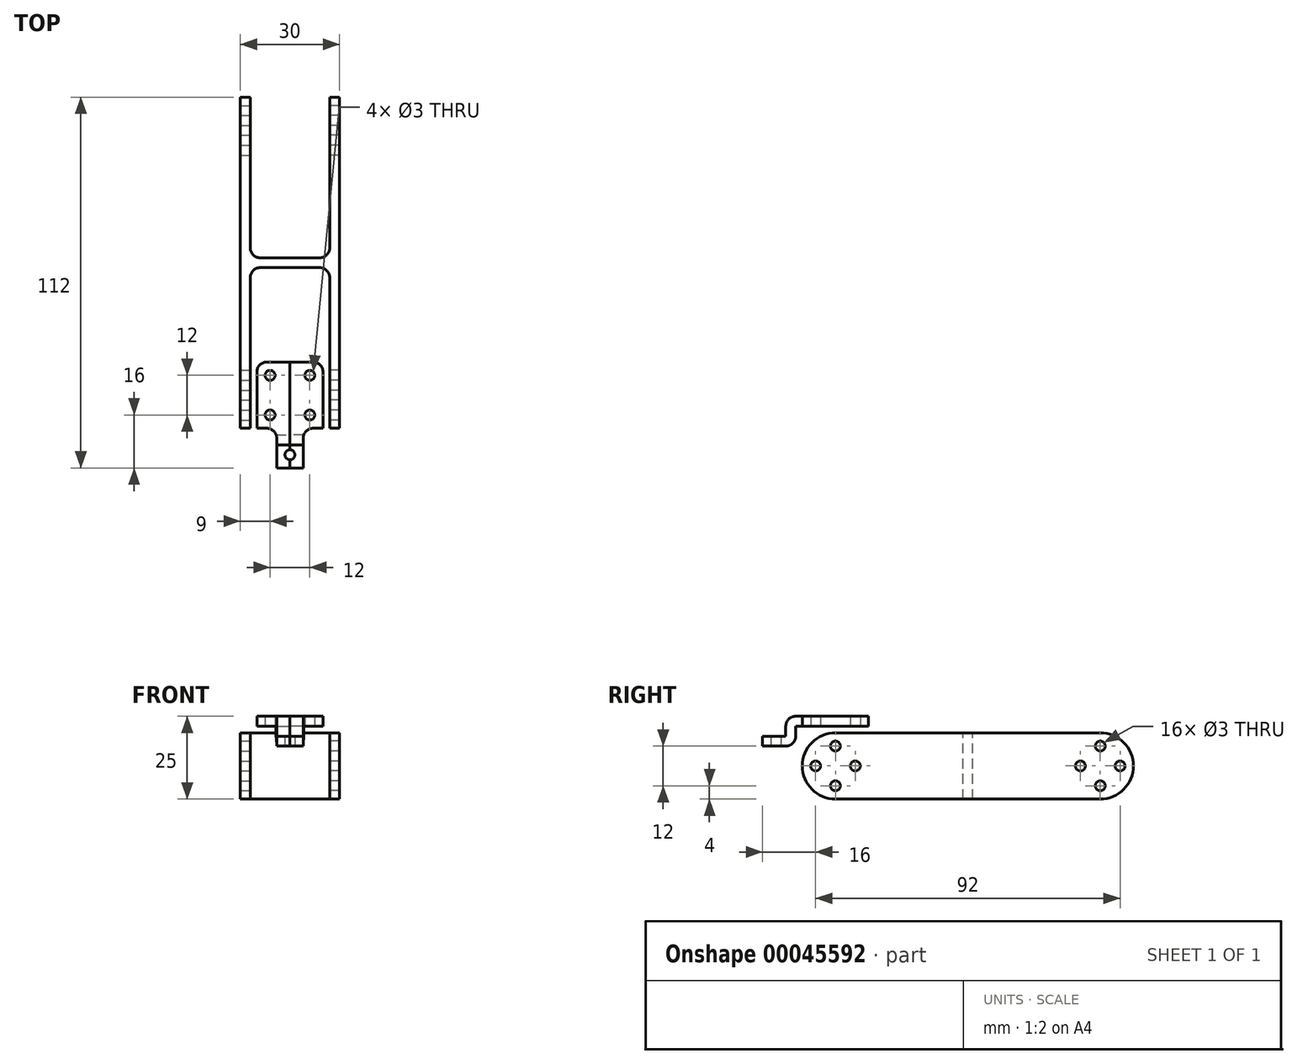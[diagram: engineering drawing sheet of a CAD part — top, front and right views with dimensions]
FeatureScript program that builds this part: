
annotation { "Feature Type Name" : "Feature", "Feature Type Description" : "" }
export const myFeature = defineFeature(function(context is Context, id is Id, definition is map)
    precondition{}
    {
        {
            var Q0;
            Q0=qCreatedBy(makeId("Right.planeOp"),FACE);
            var sketch = newSketch(context, id + "F0", { "sketchPlane" : qUnion([Q0])});
            skLineSegment(sketch, "E0.rect.bottom", {"start": v(12, 88) * mm, "end": v(-12, 88) * mm});
            skLineSegment(sketch, "E0.rect.top", {"start": v(12, 112) * mm, "end": v(-12, 112) * mm});
            skLineSegment(sketch, "E0.rect.left", {"start": v(12, 88) * mm, "end": v(12, 112) * mm});
            skLineSegment(sketch, "E0.rect.right", {"start": v(-12, 88) * mm, "end": v(-12, 112) * mm});
            skPoint(sketch, "E0.rect.middle", {"position": v(0, 100) * mm});
            skLineSegment(sketch, "E1.rect.bottom", {"start": v(-68, 88) * mm, "end": v(-92, 88) * mm});
            skLineSegment(sketch, "E1.rect.top", {"start": v(-68, 112) * mm, "end": v(-92, 112) * mm});
            skLineSegment(sketch, "E1.rect.left", {"start": v(-68, 88) * mm, "end": v(-68, 112) * mm});
            skLineSegment(sketch, "E1.rect.right", {"start": v(-92, 88) * mm, "end": v(-92, 112) * mm});
            skPoint(sketch, "E1.rect.middle", {"position": v(-80, 100) * mm});
            skLineSegment(sketch, "E2.rect.bottom", {"start": v(-92, 94) * mm, "end": v(-104, 94) * mm});
            skLineSegment(sketch, "E2.rect.top", {"start": v(-92, 106) * mm, "end": v(-104, 106) * mm});
            skLineSegment(sketch, "E2.rect.left", {"start": v(-92, 94) * mm, "end": v(-92, 106) * mm});
            skLineSegment(sketch, "E2.rect.right", {"start": v(-104, 94) * mm, "end": v(-104, 106) * mm});
            skPoint(sketch, "E2.rect.middle", {"position": v(-98, 100) * mm});
            skLineSegment(sketch, "E3", {"start": v(0, 100) * mm, "end": v(-80, 100) * mm, "construction": true});
            skLineSegment(sketch, "E4", {"start": v(-80, 100) * mm, "end": v(-98, 100) * mm, "construction": true});
            skLineSegment(sketch, "E5.rect.bottom", {"start": v(-18, 0) * mm, "end": v(18, 0) * mm});
            skLineSegment(sketch, "E5.rect.top", {"start": v(-18, -36) * mm, "end": v(18, -36) * mm});
            skLineSegment(sketch, "E5.rect.left", {"start": v(-18, 0) * mm, "end": v(-18, -36) * mm});
            skLineSegment(sketch, "E5.rect.right", {"start": v(18, 0) * mm, "end": v(18, -36) * mm});
            skPoint(sketch, "E5.rect.middle", {"position": v(0, -18) * mm});
            skCircle(sketch, "E6", {"center": v(0, 100) * mm, "radius": 6 * mm, "construction": true});
            skCircle(sketch, "E7", {"center": v(-80, 100) * mm, "radius": 6 * mm, "construction": true});
            skCircle(sketch, "E8", {"center": v(-80, 106) * mm, "radius": 1.5 * mm});
            skCircle(sketch, "E9", {"center": v(0, 106) * mm, "radius": 1.5 * mm});
            skCircle(sketch, "E10", {"center": v(-98, 100) * mm, "radius": 1.5 * mm});
            skCircle(sketch, "E11.1.0", {"center": v(-86, 100) * mm, "radius": 1.5 * mm});
            skCircle(sketch, "E11.2.0", {"center": v(-80, 94) * mm, "radius": 1.5 * mm});
            skCircle(sketch, "E11.3.0", {"center": v(-74, 100) * mm, "radius": 1.5 * mm});
            skCircle(sketch, "E12.1.0", {"center": v(-6, 100) * mm, "radius": 1.5 * mm});
            skCircle(sketch, "E12.2.0", {"center": v(0, 94) * mm, "radius": 1.5 * mm});
            skCircle(sketch, "E12.3.0", {"center": v(6, 100) * mm, "radius": 1.5 * mm});
            skLineSegment(sketch, "E13.0", {"start": v(-12, -6) * mm, "end": v(12, -6) * mm, "construction": true});
            skLineSegment(sketch, "E13.1", {"start": v(-12, -6) * mm, "end": v(-12, -30) * mm, "construction": true});
            skLineSegment(sketch, "E13.2", {"start": v(-12, -30) * mm, "end": v(12, -30) * mm, "construction": true});
            skLineSegment(sketch, "E13.3", {"start": v(12, -6) * mm, "end": v(12, -30) * mm, "construction": true});
            skCircle(sketch, "E14", {"center": v(-12, -6) * mm, "radius": 1.5 * mm});
            skCircle(sketch, "E15", {"center": v(12, -6) * mm, "radius": 1.5 * mm});
            skCircle(sketch, "E16", {"center": v(12, -30) * mm, "radius": 1.5 * mm});
            skCircle(sketch, "E17", {"center": v(-12, -30) * mm, "radius": 1.5 * mm});
            skSolve(sketch);
        }
        {
            var Q0;
            Q0=qCreatedBy(makeId("Top.planeOp"),FACE);
            var Q1;
            Q1=sQuery(id+"F0.wireOp",VERTEX,"E0.rect.middle");
            cPlane(context, id + "F1", {"entities" : qUnion([Q0, Q1]), "cplaneType" : CPlaneType.PLANE_POINT, "offset" : 150 * mm, "width" : 150 * mm, "height" : 150 * mm});
        }
        {
            var Q0;
            Q0=qCreatedBy(id+"F1.planeOp",FACE);
            var sketch = newSketch(context, id + "F2", { "sketchPlane" : qUnion([Q0])});
            skLineSegment(sketch, "E18.rect.bottom", {"start": v(12, 12) * mm, "end": v(-12, 12) * mm});
            skLineSegment(sketch, "E18.rect.top", {"start": v(12, -12) * mm, "end": v(-12, -12) * mm});
            skLineSegment(sketch, "E18.rect.left", {"start": v(12, 12) * mm, "end": v(12, -12) * mm});
            skLineSegment(sketch, "E18.rect.right", {"start": v(-12, 12) * mm, "end": v(-12, -12) * mm});
            skPoint(sketch, "E18.rect.middle", {"position": v(0, 0) * mm});
            skLineSegment(sketch, "E19.rect.bottom", {"start": v(12, -68) * mm, "end": v(-12, -68) * mm});
            skLineSegment(sketch, "E19.rect.top", {"start": v(12, -92) * mm, "end": v(-12, -92) * mm});
            skLineSegment(sketch, "E19.rect.left", {"start": v(12, -68) * mm, "end": v(12, -92) * mm});
            skLineSegment(sketch, "E19.rect.right", {"start": v(-12, -68) * mm, "end": v(-12, -92) * mm});
            skPoint(sketch, "E19.rect.middle", {"position": v(0, -80) * mm});
            skLineSegment(sketch, "E20.rect.bottom", {"start": v(6, -92) * mm, "end": v(-6, -92) * mm});
            skLineSegment(sketch, "E20.rect.top", {"start": v(6, -104) * mm, "end": v(-6, -104) * mm});
            skLineSegment(sketch, "E20.rect.left", {"start": v(6, -92) * mm, "end": v(6, -104) * mm});
            skLineSegment(sketch, "E20.rect.right", {"start": v(-6, -92) * mm, "end": v(-6, -104) * mm});
            skPoint(sketch, "E20.rect.middle", {"position": v(0, -98) * mm});
            skLineSegment(sketch, "E21.0", {"start": v(-6, -74) * mm, "end": v(-6, -86) * mm, "construction": true});
            skLineSegment(sketch, "E21.1", {"start": v(6, -74) * mm, "end": v(-6, -74) * mm, "construction": true});
            skLineSegment(sketch, "E21.2", {"start": v(6, -74) * mm, "end": v(6, -86) * mm, "construction": true});
            skLineSegment(sketch, "E21.3", {"start": v(6, -86) * mm, "end": v(-6, -86) * mm, "construction": true});
            skLineSegment(sketch, "E22.0", {"start": v(-6, 6) * mm, "end": v(-6, -6) * mm, "construction": true});
            skLineSegment(sketch, "E22.1", {"start": v(6, 6) * mm, "end": v(-6, 6) * mm, "construction": true});
            skLineSegment(sketch, "E22.2", {"start": v(6, 6) * mm, "end": v(6, -6) * mm, "construction": true});
            skLineSegment(sketch, "E22.3", {"start": v(6, -6) * mm, "end": v(-6, -6) * mm, "construction": true});
            skCircle(sketch, "E23", {"center": v(-6, -86) * mm, "radius": 1.5 * mm});
            skCircle(sketch, "E24", {"center": v(-6, -74) * mm, "radius": 1.5 * mm});
            skCircle(sketch, "E25", {"center": v(6, -86) * mm, "radius": 1.5 * mm});
            skCircle(sketch, "E26", {"center": v(0, -98) * mm, "radius": 1.5 * mm});
            skCircle(sketch, "E27", {"center": v(6, -74) * mm, "radius": 1.5 * mm});
            skCircle(sketch, "E28", {"center": v(6, -6) * mm, "radius": 1.5 * mm});
            skCircle(sketch, "E29", {"center": v(6, 6) * mm, "radius": 1.5 * mm});
            skCircle(sketch, "E30", {"center": v(-6, 6) * mm, "radius": 1.5 * mm});
            skCircle(sketch, "E31", {"center": v(-6, -6) * mm, "radius": 1.5 * mm});
            skCircle(sketch, "E32", {"center": v(0, -80) * mm, "radius": 1.5 * mm});
            skCircle(sketch, "E33", {"center": v(0, 0) * mm, "radius": 1.5 * mm});
            skSolve(sketch);
        }
        {
            var Q0;
            Q0=qCreatedBy(makeId("Top.planeOp"),FACE);
            var sketch = newSketch(context, id + "F3", { "sketchPlane" : qUnion([Q0])});
            skLineSegment(sketch, "E34.rect.bottom", {"start": v(18, 18) * mm, "end": v(-18, 18) * mm});
            skLineSegment(sketch, "E34.rect.top", {"start": v(18, -18) * mm, "end": v(-18, -18) * mm});
            skLineSegment(sketch, "E34.rect.left", {"start": v(18, 18) * mm, "end": v(18, -18) * mm});
            skLineSegment(sketch, "E34.rect.right", {"start": v(-18, 18) * mm, "end": v(-18, -18) * mm});
            skPoint(sketch, "E34.rect.middle", {"position": v(0, 0) * mm});
            skCircle(sketch, "E35", {"center": v(0, 0) * mm, "radius": 12 * mm, "construction": true});
            skCircle(sketch, "E36", {"center": v(-12, 0) * mm, "radius": 1.5 * mm});
            skCircle(sketch, "E37.1.0", {"center": v(-8.49, -8.49) * mm, "radius": 1.5 * mm});
            skCircle(sketch, "E37.2.0", {"center": v(0, -12) * mm, "radius": 1.5 * mm});
            skCircle(sketch, "E37.3.0", {"center": v(8.49, -8.49) * mm, "radius": 1.5 * mm});
            skCircle(sketch, "E37.4.0", {"center": v(12, 0) * mm, "radius": 1.5 * mm});
            skCircle(sketch, "E37.5.0", {"center": v(8.49, 8.49) * mm, "radius": 1.5 * mm});
            skCircle(sketch, "E37.6.0", {"center": v(0, 12) * mm, "radius": 1.5 * mm});
            skCircle(sketch, "E37.7.0", {"center": v(-8.49, 8.49) * mm, "radius": 1.5 * mm});
            skCircle(sketch, "E38", {"center": v(0, 0) * mm, "radius": 16 * mm});
            skSolve(sketch);
        }
        {
            var Q0;
            Q0=qCreatedBy(makeId("Front.planeOp"),FACE);
            var sketch = newSketch(context, id + "F4", { "sketchPlane" : qUnion([Q0])});
            skLineSegment(sketch, "E39.rect.bottom", {"start": v(12, 88) * mm, "end": v(-12, 88) * mm});
            skLineSegment(sketch, "E39.rect.top", {"start": v(12, 112) * mm, "end": v(-12, 112) * mm});
            skLineSegment(sketch, "E39.rect.left", {"start": v(12, 88) * mm, "end": v(12, 112) * mm});
            skLineSegment(sketch, "E39.rect.right", {"start": v(-12, 88) * mm, "end": v(-12, 112) * mm});
            skPoint(sketch, "E39.rect.middle", {"position": v(0, 100) * mm});
            skLineSegment(sketch, "E40.0", {"start": v(6, 106) * mm, "end": v(-6, 106) * mm, "construction": true});
            skLineSegment(sketch, "E40.1", {"start": v(6, 94) * mm, "end": v(6, 106) * mm, "construction": true});
            skLineSegment(sketch, "E40.2", {"start": v(6, 94) * mm, "end": v(-6, 94) * mm, "construction": true});
            skLineSegment(sketch, "E40.3", {"start": v(-6, 94) * mm, "end": v(-6, 106) * mm, "construction": true});
            skCircle(sketch, "E41", {"center": v(-6, 106) * mm, "radius": 1.5 * mm});
            skCircle(sketch, "E42", {"center": v(6, 106) * mm, "radius": 1.5 * mm});
            skCircle(sketch, "E43", {"center": v(6, 94) * mm, "radius": 1.5 * mm});
            skCircle(sketch, "E44", {"center": v(-6, 94) * mm, "radius": 1.5 * mm});
            skSolve(sketch);
        }
        {
            var Q0;
            Q0=qCreatedBy(makeId("Right.planeOp"),FACE);
            var sketch = newSketch(context, id + "F5", { "sketchPlane" : qUnion([Q0])});
            skLineSegment(sketch, "E45", {"start": v(0, 3) * mm, "end": v(-12.96, 3) * mm});
            skLineSegment(sketch, "E46", {"start": v(-12, 110) * mm, "end": v(-15, 110) * mm});
            skLineSegment(sketch, "E47", {"start": v(-16, 0) * mm, "end": v(0, 0) * mm});
            skLineSegment(sketch, "E48", {"start": v(0, 0) * mm, "end": v(0, 3) * mm});
            skLineSegment(sketch, "E49", {"start": v(-12, 110) * mm, "end": v(-12, 85) * mm});
            skLineSegment(sketch, "E50", {"start": v(-12, 85) * mm, "end": v(-12.96, 3) * mm});
            skLineSegment(sketch, "E51", {"start": v(-16, 0) * mm, "end": v(-15, 85) * mm});
            skLineSegment(sketch, "E52", {"start": v(-15, 85) * mm, "end": v(-15, 110) * mm});
            skSolve(sketch);
        }
        {
            var Q0;
            Q0=makeQuery(id+"F5.imprint","IMPRINT",FACE,{"disambiguationData":[TD([[makeQuery(id+"F5.imprint","IMPRINT",EDGE,{"derivedFrom":sQuery(id+"F5.wireOp",EDGE,"E45")}),1.0]])]});
            extrude(context, id + "F6", {"entities" : qUnion([Q0]), "depth" : 16 * mm});
        }
        {
            var Q0;
            Q0=qCreatedBy(makeId("Front.planeOp"),FACE);
            var sketch = newSketch(context, id + "F7", { "sketchPlane" : qUnion([Q0])});
            skLineSegment(sketch, "E53", {"start": v(10, 110) * mm, "end": v(10, 85) * mm});
            skLineSegment(sketch, "E54", {"start": v(10, 85) * mm, "end": v(16, 3) * mm});
            skLineSegment(sketch, "E55", {"start": v(16, 3) * mm, "end": v(16, 110) * mm});
            skLineSegment(sketch, "E56", {"start": v(16, 110) * mm, "end": v(10, 110) * mm});
            skCircle(sketch, "E57.0", {"center": v(6, 106) * mm, "radius": 1.5 * mm});
            skCircle(sketch, "E57.1", {"center": v(6, 94) * mm, "radius": 1.5 * mm});
            skSolve(sketch);
        }
        {
            var Q0;
            Q0 = qSketchRegion(id + "F7", true);
            extrude(context, id + "F8", {"entities" : qUnion([Q0]), "operationType" : NewBodyOperationType.REMOVE, "endBound" : BoundingType.THROUGH_ALL, "depth" : 25 * mm});
        }
        {
            var Q0;
            Q0=qCreatedBy(makeId("Top.planeOp"),FACE);
            var sketch = newSketch(context, id + "F9", { "sketchPlane" : qUnion([Q0])});
            skCircle(sketch, "E58.0", {"center": v(12, 0) * mm, "radius": 1.5 * mm});
            skCircle(sketch, "E58.1", {"center": v(8.49, -8.49) * mm, "radius": 1.5 * mm});
            skCircle(sketch, "E59", {"center": v(0, 0) * mm, "radius": 8 * mm});
            skSolve(sketch);
        }
        {
            var Q0;
            Q0 = qSketchRegion(id + "F9", true);
            var Q1;
            Q1=makeQuery(id+"F6.opExtrude","SWEPT_FACE",FACE,{"disambiguationData":[OSD([sQuery(id+"F5.wireOp",EDGE,"E45")])]});
            extrude(context, id + "F10", {"entities" : qUnion([Q0]), "operationType" : NewBodyOperationType.REMOVE, "endBound" : BoundingType.UP_TO_SURFACE, "endBoundEntityFace" : qUnion([Q1]), "depth" : 25 * mm});
        }
        {
            var Q0;
            Q0=makeQuery(id+"F8.boolean.opBoolean","COPY",EDGE,{"derivedFrom":makeQuery(id+"F8.opExtrude","SWEPT_EDGE",EDGE,{"disambiguationData":[OSD([sQuery(id+"F7.wireOp",EDGE,"E53"),sQuery(id+"F7.wireOp",EDGE,"E56")])]})});
            var Q1;
            Q1=makeQuery(id+"F6.opExtrude","SWEPT_EDGE",EDGE,{"disambiguationData":[OSD([sQuery(id+"F5.wireOp",EDGE,"E47"),sQuery(id+"F5.wireOp",EDGE,"E51")])]});
            var Q2;
            Q2=makeQuery(id+"F6.opExtrude","SWEPT_EDGE",EDGE,{"disambiguationData":[OSD([sQuery(id+"F5.wireOp",EDGE,"E45"),sQuery(id+"F5.wireOp",EDGE,"E50")])]});
            fillet(context, id + "F11", {"entities" : qUnion([Q0, Q1, Q2]), "radius" : 3 * mm, "tangentPropagation" : true, "allowEdgeOverflow" : false});
        }
        {
            var Q0;
            Q0=makeQuery(id+"F6.opExtrude","SWEPT_BODY",BODY,{"disambiguationData":[OSD([sQuery(id+"F5.wireOp",EDGE,"E45"),sQuery(id+"F5.wireOp",EDGE,"E46"),sQuery(id+"F5.wireOp",EDGE,"E47"),sQuery(id+"F5.wireOp",EDGE,"E48"),sQuery(id+"F5.wireOp",EDGE,"E49"),sQuery(id+"F5.wireOp",EDGE,"E50"),sQuery(id+"F5.wireOp",EDGE,"E51"),sQuery(id+"F5.wireOp",EDGE,"E52")])]});
            var Q1;
            Q1=qCreatedBy(makeId("Right.planeOp"),FACE);
            mirror(context, id + "F12", {"operationType" : NewBodyOperationType.ADD, "entities" : qUnion([Q0]), "mirrorPlane" : qUnion([Q1])});
        }
        {
            var Q0;
            Q0=makeQuery(id+"F6.opExtrude","SWEPT_BODY",BODY,{"disambiguationData":[OSD([sQuery(id+"F5.wireOp",EDGE,"E45"),sQuery(id+"F5.wireOp",EDGE,"E46"),sQuery(id+"F5.wireOp",EDGE,"E47"),sQuery(id+"F5.wireOp",EDGE,"E48"),sQuery(id+"F5.wireOp",EDGE,"E49"),sQuery(id+"F5.wireOp",EDGE,"E50"),sQuery(id+"F5.wireOp",EDGE,"E51"),sQuery(id+"F5.wireOp",EDGE,"E52")])]});
            var Q1;
            Q1=qCreatedBy(makeId("Front.planeOp"),FACE);
            mirror(context, id + "F13", {"operationType" : NewBodyOperationType.ADD, "entities" : qUnion([Q0]), "mirrorPlane" : qUnion([Q1])});
        }
        {
            var Q0;
            Q0=qCreatedBy(makeId("Right.planeOp"),FACE);
            var sketch = newSketch(context, id + "F14", { "sketchPlane" : qUnion([Q0])});
            skLineSegment(sketch, "E60.rect.bottom", {"start": v(-80, 90) * mm, "end": v(0, 90) * mm});
            skLineSegment(sketch, "E60.rect.top", {"start": v(-80, 110) * mm, "end": v(0, 110) * mm});
            skLineSegment(sketch, "E60.rect.left", {"start": v(-80, 90) * mm, "end": v(-80, 110) * mm, "construction": true});
            skLineSegment(sketch, "E60.rect.right", {"start": v(0, 90) * mm, "end": v(0, 110) * mm, "construction": true});
            skPoint(sketch, "E60.rect.middle", {"position": v(-40, 100) * mm});
            skArc(sketch, "E61", {"start": v(-80, 110) * mm, "mid": v(-90, 100) * mm, "end": v(-80, 90) * mm});
            skArc(sketch, "E62", {"start": v(0, 90) * mm, "mid": v(10, 100) * mm, "end": v(0, 110) * mm});
            skCircle(sketch, "E63.0", {"center": v(-80, 106) * mm, "radius": 1.5 * mm});
            skCircle(sketch, "E63.1", {"center": v(-86, 100) * mm, "radius": 1.5 * mm});
            skCircle(sketch, "E63.2", {"center": v(-80, 94) * mm, "radius": 1.5 * mm});
            skCircle(sketch, "E63.3", {"center": v(-74, 100) * mm, "radius": 1.5 * mm});
            skCircle(sketch, "E63.4", {"center": v(0, 106) * mm, "radius": 1.5 * mm});
            skCircle(sketch, "E63.5", {"center": v(-6, 100) * mm, "radius": 1.5 * mm});
            skCircle(sketch, "E63.6", {"center": v(0, 94) * mm, "radius": 1.5 * mm});
            skCircle(sketch, "E63.7", {"center": v(6, 100) * mm, "radius": 1.5 * mm});
            skSolve(sketch);
        }
        {
            var Q0;
            Q0 = qSketchRegion(id + "F14", true);
            extrude(context, id + "F15", {"entities" : qUnion([Q0]), "depth" : (12 + 3) * mm});
        }
        {
            var Q0;
            Q0=qCreatedBy(id+"F1.planeOp",FACE);
            var sketch = newSketch(context, id + "F16", { "sketchPlane" : qUnion([Q0])});
            skLineSegment(sketch, "E64", {"start": v(15, -90) * mm, "end": v(12, -90) * mm});
            skLineSegment(sketch, "E65", {"start": v(12, -90) * mm, "end": v(12, -44.5) * mm});
            skLineSegment(sketch, "E66", {"start": v(9, -41.5) * mm, "end": v(0, -41.5) * mm});
            skLineSegment(sketch, "E67", {"start": v(0, -41.5) * mm, "end": v(0, -38.5) * mm});
            skLineSegment(sketch, "E68", {"start": v(0, -38.5) * mm, "end": v(9, -38.5) * mm});
            skLineSegment(sketch, "E69", {"start": v(12, -35.5) * mm, "end": v(12, 10) * mm});
            skLineSegment(sketch, "E70", {"start": v(12, 10) * mm, "end": v(15, 10) * mm});
            skLineSegment(sketch, "E71", {"start": v(15, 10) * mm, "end": v(15, -90) * mm});
            skLineSegment(sketch, "E72", {"start": v(12, -90) * mm, "end": v(0, -90) * mm, "construction": true});
            skPoint(sketch, "E73.visualSharp", {"position": v(12, -38.5) * mm});
            skArc(sketch, "E73.filletArc", {"start": v(9, -38.5) * mm, "mid": v(11.12, -37.62) * mm, "end": v(12, -35.5) * mm});
            skPoint(sketch, "E74.visualSharp", {"position": v(12, -41.5) * mm});
            skArc(sketch, "E74.filletArc", {"start": v(12, -44.5) * mm, "mid": v(11.12, -42.38) * mm, "end": v(9, -41.5) * mm});
            skLineSegment(sketch, "E75", {"start": v(12, 10) * mm, "end": v(0, 10) * mm, "construction": true});
            skSolve(sketch);
        }
        {
            var Q0;
            Q0 = qSketchRegion(id + "F16", true);
            extrude(context, id + "F17", {"entities" : qUnion([Q0]), "operationType" : NewBodyOperationType.INTERSECT, "oppositeDirection" : true, "depth" : 25 * mm, "hasSecondDirection" : true, "secondDirectionOppositeDirection" : false, "secondDirectionDepth" : 25 * mm});
        }
        {
            var Q0;
            Q0=makeQuery(id+"F15.opExtrude","SWEPT_BODY",BODY,{"disambiguationData":[OSD([sQuery(id+"F14.wireOp",EDGE,"E60.rect.bottom"),sQuery(id+"F14.wireOp",EDGE,"E60.rect.top"),sQuery(id+"F14.wireOp",EDGE,"E61"),sQuery(id+"F14.wireOp",EDGE,"E62"),sQuery(id+"F14.wireOp",EDGE,"E63.0"),sQuery(id+"F14.wireOp",EDGE,"E63.1"),sQuery(id+"F14.wireOp",EDGE,"E63.2"),sQuery(id+"F14.wireOp",EDGE,"E63.3"),sQuery(id+"F14.wireOp",EDGE,"E63.4"),sQuery(id+"F14.wireOp",EDGE,"E63.5"),sQuery(id+"F14.wireOp",EDGE,"E63.6"),sQuery(id+"F14.wireOp",EDGE,"E63.7")])]});
            var Q1;
            Q1=qCreatedBy(makeId("Right.planeOp"),FACE);
            mirror(context, id + "F18", {"operationType" : NewBodyOperationType.ADD, "entities" : qUnion([Q0]), "mirrorPlane" : qUnion([Q1])});
        }
        {
            var Q0;
            Q0=qCreatedBy(makeId("Right.planeOp"),FACE);
            var sketch = newSketch(context, id + "F19", { "sketchPlane" : qUnion([Q0])});
            skLineSegment(sketch, "E76.0", {"start": v(-95, 109) * mm, "end": v(-102, 109) * mm});
            skLineSegment(sketch, "E77.0", {"start": v(-70, 115) * mm, "end": v(-92, 115) * mm});
            skLineSegment(sketch, "E77.1", {"start": v(-95, 109) * mm, "end": v(-95, 112) * mm});
            skLineSegment(sketch, "E78.0", {"start": v(-95, 106) * mm, "end": v(-102, 106) * mm});
            skLineSegment(sketch, "E78.1", {"start": v(-92, 109) * mm, "end": v(-92, 112) * mm});
            skLineSegment(sketch, "E78.2", {"start": v(-70, 112) * mm, "end": v(-92, 112) * mm});
            skPoint(sketch, "E79.orphan", {"position": v(-92, 88) * mm});
            skLineSegment(sketch, "E80", {"start": v(-102, 109) * mm, "end": v(-102, 106) * mm});
            skPoint(sketch, "E81.orphan", {"position": v(-104, 106) * mm});
            skLineSegment(sketch, "E82", {"start": v(-70, 115) * mm, "end": v(-70, 112) * mm});
            skPoint(sketch, "E83.orphan", {"position": v(-68, 112) * mm});
            skPoint(sketch, "E84.visualSharp", {"position": v(-95, 115) * mm});
            skArc(sketch, "E84.filletArc", {"start": v(-92, 115) * mm, "mid": v(-94.12, 114.12) * mm, "end": v(-95, 112) * mm});
            skPoint(sketch, "E85.visualSharp", {"position": v(-92, 106) * mm});
            skArc(sketch, "E85.filletArc", {"start": v(-95, 106) * mm, "mid": v(-92.88, 106.88) * mm, "end": v(-92, 109) * mm});
            skSolve(sketch);
        }
        {
            var Q0;
            Q0=makeQuery(id+"F19.imprint","IMPRINT",FACE,{"disambiguationData":[TD([[makeQuery(id+"F19.imprint","IMPRINT",EDGE,{"derivedFrom":sQuery(id+"F19.wireOp",EDGE,"E76.0")}),1.0]])]});
            extrude(context, id + "F20", {"entities" : qUnion([Q0]), "depth" : 10 * mm});
        }
        {
            var Q0;
            Q0=qCreatedBy(id+"F1.planeOp",FACE);
            var sketch = newSketch(context, id + "F21", { "sketchPlane" : qUnion([Q0])});
            skCircle(sketch, "E86.0", {"center": v(0, -98) * mm, "radius": 1.5 * mm});
            skCircle(sketch, "E86.1", {"center": v(6, -86) * mm, "radius": 1.5 * mm});
            skCircle(sketch, "E86.2", {"center": v(6, -74) * mm, "radius": 1.5 * mm});
            skLineSegment(sketch, "E87", {"start": v(4, -102) * mm, "end": v(4, -93) * mm});
            skLineSegment(sketch, "E88", {"start": v(7, -90) * mm, "end": v(10, -90) * mm});
            skLineSegment(sketch, "E89", {"start": v(10, -90) * mm, "end": v(10, -102) * mm});
            skLineSegment(sketch, "E90", {"start": v(10, -102) * mm, "end": v(4, -102) * mm});
            skPoint(sketch, "E91.visualSharp", {"position": v(4, -90) * mm});
            skArc(sketch, "E91.filletArc", {"start": v(7, -90) * mm, "mid": v(4.88, -90.88) * mm, "end": v(4, -93) * mm});
            skSolve(sketch);
        }
        {
            var Q0;
            Q0 = qSketchRegion(id + "F21", true);
            extrude(context, id + "F22", {"entities" : qUnion([Q0]), "operationType" : NewBodyOperationType.REMOVE, "depth" : 25 * mm});
        }
        {
            var Q0;
            Q0=makeQuery(id+"F22.boolean.opBoolean","COPY",EDGE,{"derivedFrom":makeQuery(id+"F22.opExtrude","SWEPT_EDGE",EDGE,{"disambiguationData":[OSD([sQuery(id+"F21.wireOp",EDGE,"E88"),sQuery(id+"F21.wireOp",EDGE,"E89")])]})});
            var Q1;
            Q1=makeQuery(id+"F20.opExtrude","CAP_EDGE",EDGE,{"disambiguationData":[OSD([sQuery(id+"F19.wireOp",EDGE,"E82")])],"isStart":false});
            var Q2;
            Q2=makeQuery(id+"F22.boolean.opBoolean","COPY",EDGE,{"derivedFrom":makeQuery(id+"F22.opExtrude","SWEPT_EDGE",EDGE,{"disambiguationData":[OSD([sQuery(id+"F21.wireOp",EDGE,"E87"),sQuery(id+"F21.wireOp",EDGE,"E90")])]})});
            fillet(context, id + "F23", {"entities" : qUnion([Q0, Q1, Q2]), "radius" : 3 * mm, "tangentPropagation" : true, "allowEdgeOverflow" : false});
        }
        {
            var Q0;
            Q0=makeQuery(id+"F20.opExtrude","SWEPT_BODY",BODY,{"disambiguationData":[OSD([sQuery(id+"F19.wireOp",EDGE,"E76.0"),sQuery(id+"F19.wireOp",EDGE,"E77.0"),sQuery(id+"F19.wireOp",EDGE,"E77.1"),sQuery(id+"F19.wireOp",EDGE,"E78.0"),sQuery(id+"F19.wireOp",EDGE,"E78.1"),sQuery(id+"F19.wireOp",EDGE,"E78.2"),sQuery(id+"F19.wireOp",EDGE,"E80"),sQuery(id+"F19.wireOp",EDGE,"E82"),sQuery(id+"F19.wireOp",EDGE,"E84.filletArc"),sQuery(id+"F19.wireOp",EDGE,"E85.filletArc")])]});
            var Q1;
            Q1=qCreatedBy(makeId("Right.planeOp"),FACE);
            mirror(context, id + "F24", {"operationType" : NewBodyOperationType.ADD, "entities" : qUnion([Q0]), "mirrorPlane" : qUnion([Q1])});
        }
    });
